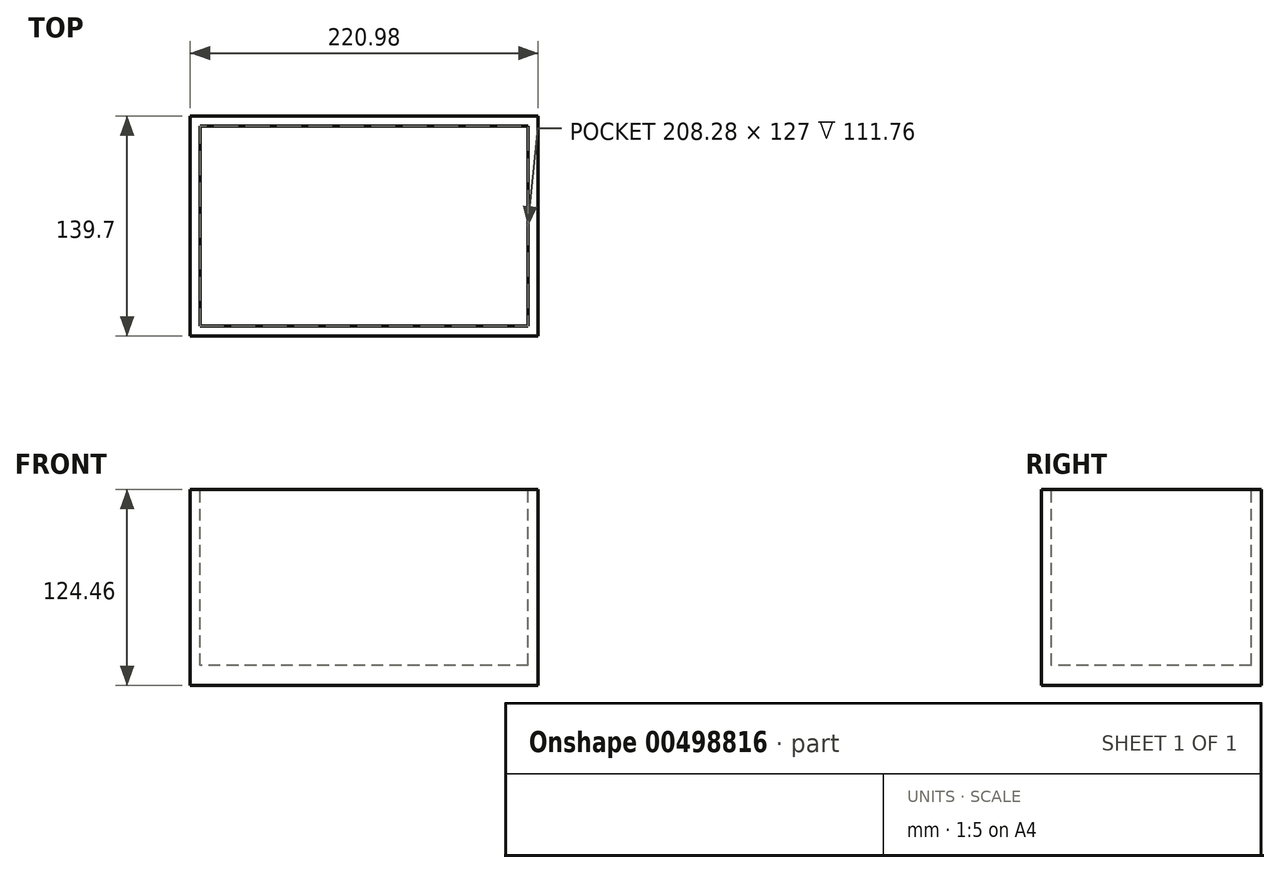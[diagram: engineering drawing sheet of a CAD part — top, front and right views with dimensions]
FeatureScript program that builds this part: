
annotation { "Feature Type Name" : "Feature", "Feature Type Description" : "" }
export const myFeature = defineFeature(function(context is Context, id is Id, definition is map)
    precondition{}
    {
        {
            var Q0;
            Q0=qCreatedBy(makeId("Top.planeOp"),FACE);
            var sketch = newSketch(context, id + "F0", { "sketchPlane" : qUnion([Q0])});
            skLineSegment(sketch, "E0.bottom", {"start": v(0, 0) * mm, "end": v(220.98, 0) * mm});
            skLineSegment(sketch, "E0.top", {"start": v(0, -139.7) * mm, "end": v(220.98, -139.7) * mm});
            skLineSegment(sketch, "E0.left", {"start": v(0, 0) * mm, "end": v(0, -139.7) * mm});
            skLineSegment(sketch, "E0.right", {"start": v(220.98, 0) * mm, "end": v(220.98, -139.7) * mm});
            skSolve(sketch);
        }
        {
            var Q0;
            Q0=makeQuery(id+"F0.imprint","IMPRINT",FACE,{"disambiguationData":[TD([[makeQuery(id+"F0.imprint","IMPRINT",EDGE,{"derivedFrom":sQuery(id+"F0.wireOp",EDGE,"E0.bottom")}),-1.0]])]});
            extrude(context, id + "F1", {"entities" : qUnion([Q0]), "depth" : 124.46 * mm});
        }
        {
            var Q0;
            Q0=makeQuery(id+"F1.opExtrude","CAP_FACE",FACE,{"disambiguationData":[OSD([sQuery(id+"F0.wireOp",EDGE,"E0.bottom"),sQuery(id+"F0.wireOp",EDGE,"E0.top"),sQuery(id+"F0.wireOp",EDGE,"E0.left"),sQuery(id+"F0.wireOp",EDGE,"E0.right")])],"isStart":false});
            var sketch = newSketch(context, id + "F2", { "sketchPlane" : qUnion([Q0])});
            skLineSegment(sketch, "E1.0.0", {"start": v(0, 0) * mm, "end": v(0, -139.7) * mm});
            skLineSegment(sketch, "E1.0.1", {"start": v(0, -139.7) * mm, "end": v(220.98, -139.7) * mm});
            skLineSegment(sketch, "E1.0.2", {"start": v(220.98, -139.7) * mm, "end": v(220.98, 0) * mm});
            skLineSegment(sketch, "E1.0.3", {"start": v(220.98, 0) * mm, "end": v(0, 0) * mm});
            skLineSegment(sketch, "E2.0", {"start": v(6.35, -6.35) * mm, "end": v(6.35, -133.35) * mm});
            skLineSegment(sketch, "E2.1", {"start": v(214.63, -6.35) * mm, "end": v(6.35, -6.35) * mm});
            skLineSegment(sketch, "E2.2", {"start": v(214.63, -133.35) * mm, "end": v(214.63, -6.35) * mm});
            skLineSegment(sketch, "E2.3", {"start": v(6.35, -133.35) * mm, "end": v(214.63, -133.35) * mm});
            skSolve(sketch);
        }
        {
            var Q0;
            Q0=makeQuery(id+"F2.imprint","IMPRINT",FACE,{"disambiguationData":[TD([[makeQuery(id+"F2.imprint","IMPRINT",EDGE,{"derivedFrom":sQuery(id+"F2.wireOp",EDGE,"E2.0")}),1.0]])]});
            extrude(context, id + "F3", {"entities" : qUnion([Q0]), "operationType" : NewBodyOperationType.REMOVE, "oppositeDirection" : true, "depth" : 111.76 * mm});
        }
    });
